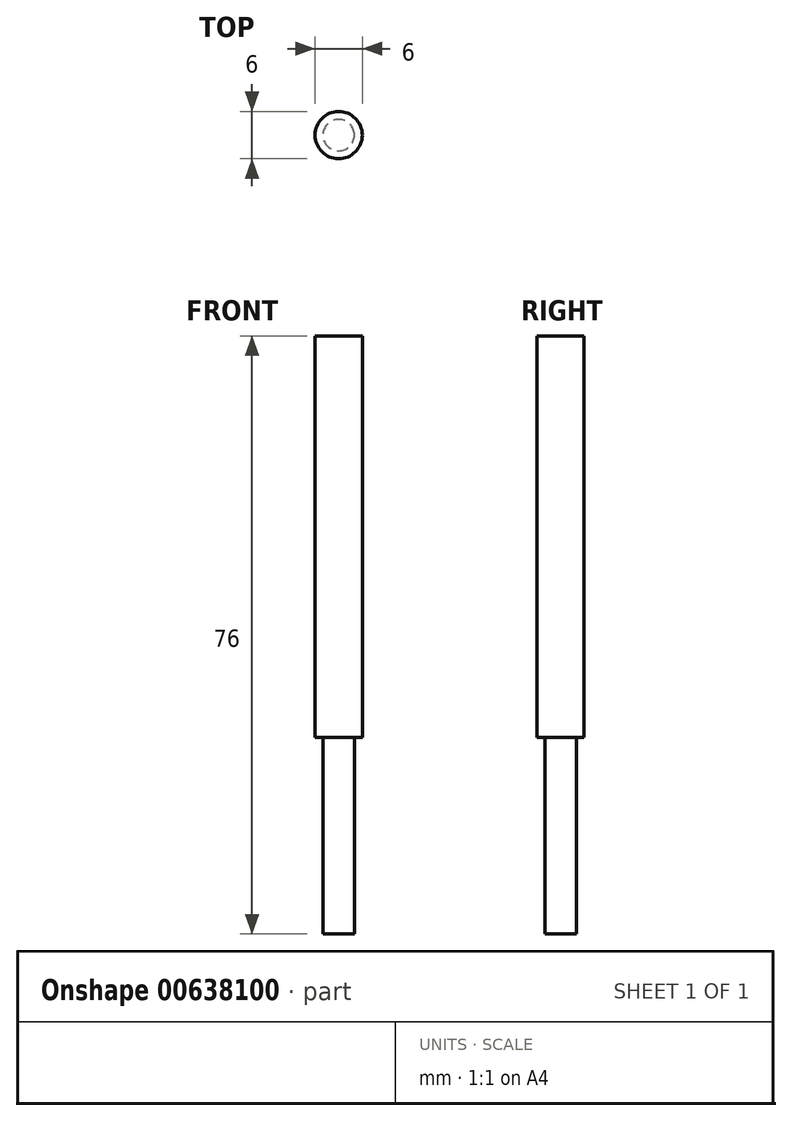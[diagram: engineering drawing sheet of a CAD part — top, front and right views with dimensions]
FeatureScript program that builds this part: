
annotation { "Feature Type Name" : "Feature", "Feature Type Description" : "" }
export const myFeature = defineFeature(function(context is Context, id is Id, definition is map)
    precondition{}
    {
        {
            var Q0;
            Q0=qCreatedBy(makeId("Top.planeOp"),FACE);
            var sketch = newSketch(context, id + "F0", { "sketchPlane" : qUnion([Q0])});
            skCircle(sketch, "E0", {"center": v(0, 0) * mm, "radius": 3 * mm});
            skSolve(sketch);
        }
        {
            var Q0;
            Q0=makeQuery(id+"F0.imprint","IMPRINT",FACE,{"disambiguationData":[TD([[makeQuery(id+"F0.imprint","IMPRINT",EDGE,{"derivedFrom":sQuery(id+"F0.wireOp",EDGE,"E0")}),1.0]])]});
            var Q1;
            Q1=sQuery(id+"F0.wireOp",EDGE,"E0");
            extrude(context, id + "F1", {"entities" : qUnion([Q0]), "surfaceEntities" : qUnion([Q1]), "depth" : 51 * mm, "offsetDistance" : 25 * mm});
        }
        {
            var Q0;
            Q0=makeQuery(id+"F1.opExtrude","CAP_FACE",FACE,{"disambiguationData":[OSD([sQuery(id+"F0.wireOp",EDGE,"E0")])],"isStart":true});
            var sketch = newSketch(context, id + "F2", { "sketchPlane" : qUnion([Q0])});
            skCircle(sketch, "E1", {"center": v(0, 0) * mm, "radius": 2 * mm});
            skSolve(sketch);
        }
        {
            var Q0;
            Q0=makeQuery(id+"F2.imprint","IMPRINT",FACE,{"disambiguationData":[TD([[makeQuery(id+"F2.imprint","IMPRINT",EDGE,{"derivedFrom":sQuery(id+"F2.wireOp",EDGE,"E1")}),1.0]])]});
            extrude(context, id + "F3", {"entities" : qUnion([Q0]), "operationType" : NewBodyOperationType.ADD, "depth" : 25 * mm, "offsetDistance" : 25 * mm});
        }
    });
